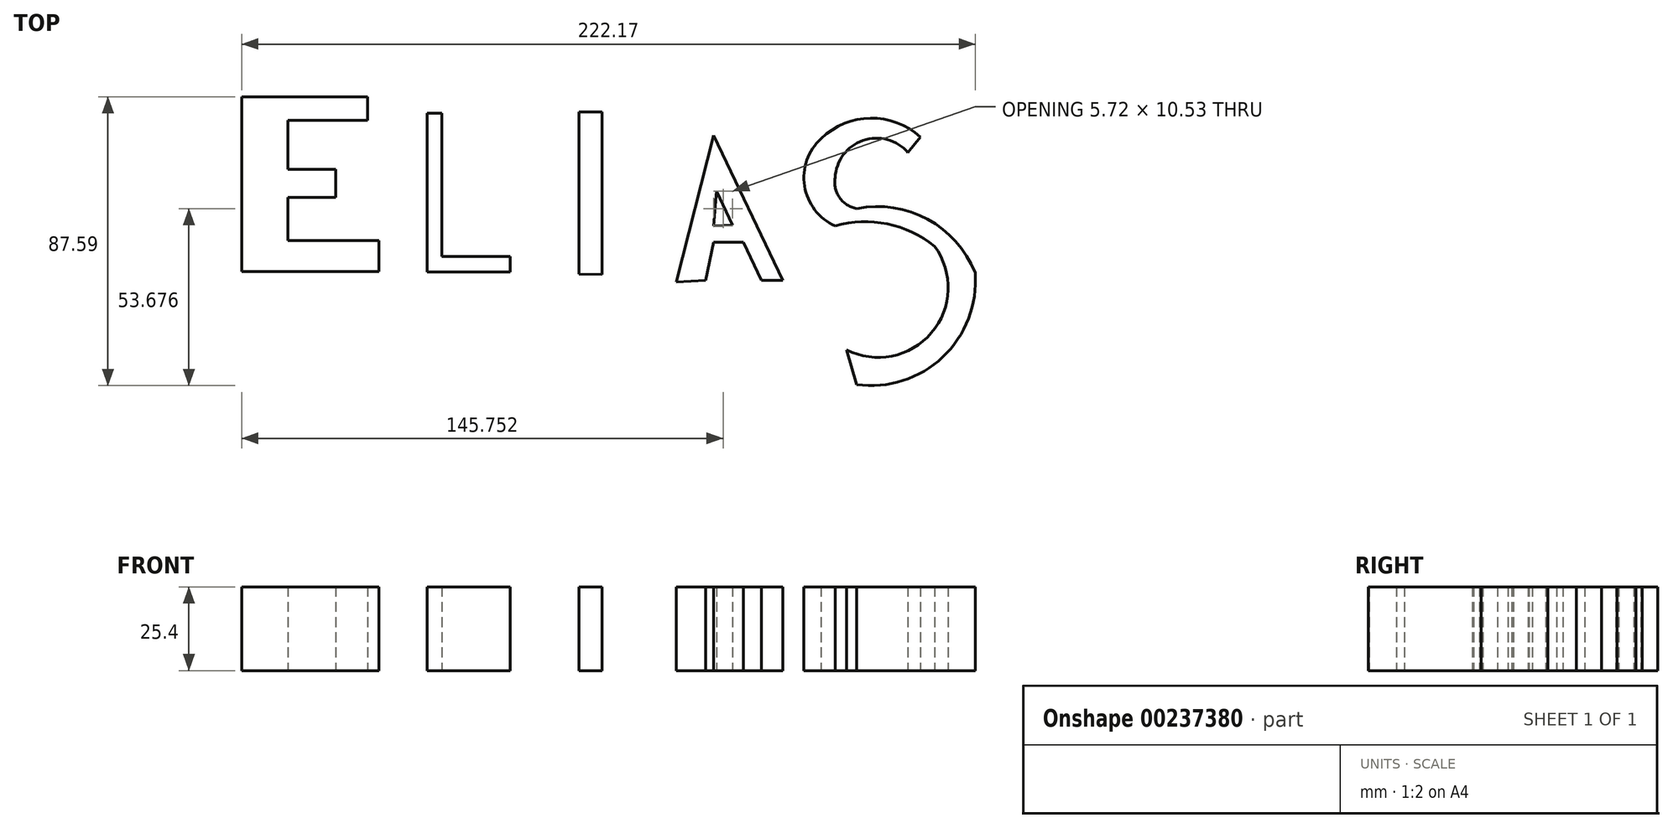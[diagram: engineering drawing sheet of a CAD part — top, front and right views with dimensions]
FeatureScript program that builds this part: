
annotation { "Feature Type Name" : "Feature", "Feature Type Description" : "" }
export const myFeature = defineFeature(function(context is Context, id is Id, definition is map)
    precondition{}
    {
        {
            var Q0;
            Q0=qCreatedBy(makeId("Top.planeOp"),FACE);
            var sketch = newSketch(context, id + "F0", { "sketchPlane" : qUnion([Q0])});
            skLineSegment(sketch, "E0", {"start": v(-45.93, 34.19) * mm, "end": v(-45.93, -14) * mm});
            skLineSegment(sketch, "E1", {"start": v(-45.93, -14) * mm, "end": v(-20.73, -14) * mm});
            skLineSegment(sketch, "E2", {"start": v(-20.73, -14) * mm, "end": v(-20.73, -9.3) * mm});
            skLineSegment(sketch, "E3", {"start": v(-20.73, -9.3) * mm, "end": v(-41.5, -9.3) * mm});
            skLineSegment(sketch, "E4", {"start": v(-41.5, -9.3) * mm, "end": v(-41.5, 34.19) * mm});
            skLineSegment(sketch, "E5", {"start": v(-41.5, 34.19) * mm, "end": v(-45.93, 34.19) * mm});
            skSolve(sketch);
        }
        {
            var Q0;
            Q0=qCreatedBy(makeId("Top.planeOp"),FACE);
            var sketch = newSketch(context, id + "F1", { "sketchPlane" : qUnion([Q0])});
            skLineSegment(sketch, "E6", {"start": v(0, -14.58) * mm, "end": v(0, 34.58) * mm});
            skLineSegment(sketch, "E7", {"start": v(0, 34.58) * mm, "end": v(7.03, 34.58) * mm});
            skLineSegment(sketch, "E8", {"start": v(7.03, 34.58) * mm, "end": v(7.03, -14.77) * mm});
            skLineSegment(sketch, "E9", {"start": v(7.03, -14.77) * mm, "end": v(0, -14.58) * mm});
            skSolve(sketch);
        }
        {
            var Q0;
            Q0=qCreatedBy(makeId("Top.planeOp"),FACE);
            var sketch = newSketch(context, id + "F2", { "sketchPlane" : qUnion([Q0])});
            skLineSegment(sketch, "E10", {"start": v(29.44, -16.97) * mm, "end": v(40.81, 27.38) * mm});
            skLineSegment(sketch, "E11", {"start": v(40.81, 27.38) * mm, "end": v(61.76, -16.53) * mm});
            skLineSegment(sketch, "E12", {"start": v(61.76, -16.53) * mm, "end": v(55.3, -16.53) * mm});
            skLineSegment(sketch, "E13", {"start": v(55.3, -16.53) * mm, "end": v(49.77, -4.94) * mm});
            skLineSegment(sketch, "E14", {"start": v(49.77, -4.94) * mm, "end": v(40.81, -4.94) * mm});
            skLineSegment(sketch, "E15", {"start": v(40.81, -4.94) * mm, "end": v(38.36, -16.53) * mm});
            skLineSegment(sketch, "E16", {"start": v(38.36, -16.53) * mm, "end": v(29.44, -16.97) * mm});
            skLineSegment(sketch, "E17", {"start": v(40.81, 0) * mm, "end": v(46.53, 0.29) * mm});
            skLineSegment(sketch, "E18", {"start": v(46.53, 0.29) * mm, "end": v(41.64, 10.53) * mm});
            skLineSegment(sketch, "E19", {"start": v(41.64, 10.53) * mm, "end": v(40.81, 0) * mm});
            skSolve(sketch);
        }
        {
            var Q0;
            Q0=makeQuery(id+"F2.imprint","IMPRINT",FACE,{"disambiguationData":[TD([[makeQuery(id+"F2.imprint","IMPRINT",EDGE,{"derivedFrom":sQuery(id+"F2.wireOp",EDGE,"E10")}),-1.0]])]});
            extrude(context, id + "F3", {"entities" : qUnion([Q0]), "depth" : 25.4 * mm});
        }
        {
            var Q0;
            Q0=makeQuery(id+"F1.imprint","IMPRINT",FACE,{"disambiguationData":[TD([[makeQuery(id+"F1.imprint","IMPRINT",EDGE,{"derivedFrom":sQuery(id+"F1.wireOp",EDGE,"E6")}),-1.0]])]});
            extrude(context, id + "F4", {"entities" : qUnion([Q0]), "depth" : 25.4 * mm});
        }
        {
            var Q0;
            Q0=makeQuery(id+"F0.imprint","IMPRINT",FACE,{"disambiguationData":[TD([[makeQuery(id+"F0.imprint","IMPRINT",EDGE,{"derivedFrom":sQuery(id+"F0.wireOp",EDGE,"E0")}),1.0]])]});
            extrude(context, id + "F5", {"entities" : qUnion([Q0]), "depth" : 25.4 * mm});
        }
        {
            var Q0;
            Q0=qCreatedBy(makeId("Top.planeOp"),FACE);
            var sketch = newSketch(context, id + "F6", { "sketchPlane" : qUnion([Q0])});
            skLineSegment(sketch, "E20", {"start": v(-60.55, -13.8) * mm, "end": v(-102.08, -13.8) * mm});
            skLineSegment(sketch, "E21", {"start": v(-102.08, -13.8) * mm, "end": v(-102.08, 39.18) * mm});
            skLineSegment(sketch, "E22", {"start": v(-102.08, 39.18) * mm, "end": v(-63.94, 39.18) * mm});
            skLineSegment(sketch, "E23", {"start": v(-63.94, 39.18) * mm, "end": v(-63.94, 31.97) * mm});
            skLineSegment(sketch, "E24", {"start": v(-63.94, 31.97) * mm, "end": v(-88.1, 31.97) * mm});
            skLineSegment(sketch, "E25", {"start": v(-88.1, 31.97) * mm, "end": v(-88.1, 17.14) * mm});
            skLineSegment(sketch, "E26", {"start": v(-88.1, 17.14) * mm, "end": v(-73.68, 17.14) * mm});
            skLineSegment(sketch, "E27", {"start": v(-73.68, 17.14) * mm, "end": v(-73.68, 8.67) * mm});
            skLineSegment(sketch, "E28", {"start": v(-73.68, 8.67) * mm, "end": v(-88.1, 8.67) * mm});
            skLineSegment(sketch, "E29", {"start": v(-88.1, 8.67) * mm, "end": v(-88.1, -4.47) * mm});
            skLineSegment(sketch, "E30", {"start": v(-88.1, -4.47) * mm, "end": v(-60.55, -4.47) * mm});
            skLineSegment(sketch, "E31", {"start": v(-60.55, -4.47) * mm, "end": v(-60.55, -13.8) * mm});
            skArc(sketch, "E32", {"start": v(103.46, 26.89) * mm, "mid": v(88.33, 32.66) * mm, "end": v(73.37, 26.47) * mm});
            skArc(sketch, "E33", {"start": v(73.37, 26.47) * mm, "mid": v(68.33, 12.09) * mm, "end": v(77.6, 0) * mm});
            skArc(sketch, "E34", {"start": v(107.7, -6.17) * mm, "mid": v(93.4, 0.58) * mm, "end": v(77.6, 0) * mm});
            skArc(sketch, "E35", {"start": v(81, -37.53) * mm, "mid": v(106.77, -32.42) * mm, "end": v(107.7, -6.17) * mm});
            skArc(sketch, "E36", {"start": v(99.64, 22.23) * mm, "mid": v(86.04, 25.91) * mm, "end": v(77.6, 14.62) * mm});
            skArc(sketch, "E37", {"start": v(77.6, 14.62) * mm, "mid": v(78.93, 8.59) * mm, "end": v(84.15, 5.28) * mm});
            skArc(sketch, "E38", {"start": v(119.98, -14.22) * mm, "mid": v(105.6, 2.03) * mm, "end": v(84.15, 5.28) * mm});
            skArc(sketch, "E39", {"start": v(84.15, -48.12) * mm, "mid": v(110.2, -39.76) * mm, "end": v(119.98, -14.22) * mm});
            skLineSegment(sketch, "E40", {"start": v(103.46, 26.89) * mm, "end": v(99.64, 22.23) * mm});
            skLineSegment(sketch, "E41", {"start": v(81, -37.53) * mm, "end": v(84.15, -48.12) * mm});
            skSolve(sketch);
        }
        {
            var Q0;
            Q0=makeQuery(id+"F6.imprint","IMPRINT",FACE,{"disambiguationData":[TD([[makeQuery(id+"F6.imprint","IMPRINT",EDGE,{"derivedFrom":sQuery(id+"F6.wireOp",EDGE,"E20")}),-1.0]])]});
            extrude(context, id + "F7", {"entities" : qUnion([Q0]), "depth" : 25.4 * mm});
        }
        {
            var Q0;
            Q0=makeQuery(id+"F6.imprint","IMPRINT",FACE,{"disambiguationData":[TD([[makeQuery(id+"F6.imprint","IMPRINT",EDGE,{"derivedFrom":sQuery(id+"F6.wireOp",EDGE,"E32")}),1.0]])]});
            extrude(context, id + "F8", {"entities" : qUnion([Q0]), "depth" : 25.4 * mm});
        }
    });
